annotation { "Feature Type Name" : "Feature", "Feature Type Description" : "" }
export const myFeature = defineFeature(function(context is Context, id is Id, definition is map)
    precondition{}
    {
        {
            var Q0;
            Q0=qCreatedBy(makeId("Front.planeOp"),FACE);
            var sketch = newSketch(context, id + "F0", { "sketchPlane" : qUnion([Q0])});
            skLineSegment(sketch, "E0", {"start": v(-28.04, -14.03) * mm, "end": v(-24.95, -14.03) * mm});
            skLineSegment(sketch, "E1", {"start": v(-24.95, -14.03) * mm, "end": v(-22.4, -16.57) * mm});
            skLineSegment(sketch, "E2", {"start": v(-22.4, -16.57) * mm, "end": v(-22.4, -21.02) * mm});
            skLineSegment(sketch, "E3", {"start": v(-22.4, -21.02) * mm, "end": v(-24.95, -23.56) * mm});
            skLineSegment(sketch, "E4", {"start": v(-24.95, -23.56) * mm, "end": v(-40.78, -23.56) * mm});
            skLineSegment(sketch, "E5", {"start": v(-40.78, -23.56) * mm, "end": v(-40.78, -46.8) * mm});
            skLineSegment(sketch, "E6", {"start": v(0, 62.15) * mm, "end": v(0, 0) * mm, "construction": true});
            skLineSegment(sketch, "E7.MirrorCS", {"start": v(22.4, -21.02) * mm, "end": v(24.95, -23.56) * mm});
            skLineSegment(sketch, "E8.MirrorCS", {"start": v(24.95, -14.03) * mm, "end": v(22.4, -16.57) * mm});
            skLineSegment(sketch, "E9.MirrorCS", {"start": v(22.4, -16.57) * mm, "end": v(22.4, -21.02) * mm});
            skLineSegment(sketch, "E10.MirrorCS", {"start": v(40.78, -23.56) * mm, "end": v(40.78, -46.8) * mm});
            skLineSegment(sketch, "E11.MirrorCS", {"start": v(24.95, -23.56) * mm, "end": v(40.78, -23.56) * mm});
            skLineSegment(sketch, "E12.MirrorCS", {"start": v(28.04, -14.03) * mm, "end": v(24.95, -14.03) * mm});
            skArc(sketch, "E13.trimOffspring", {"start": v(40.73, -1.93) * mm, "mid": v(0, 40.78) * mm, "end": v(-40.73, -1.93) * mm});
            skPoint(sketch, "E14.center.orphan", {"position": v(0, 19.4) * mm});
            skLineSegment(sketch, "E15", {"start": v(-40.78, -46.8) * mm, "end": v(40.78, -46.8) * mm});
            skPoint(sketch, "E16.visualSharp", {"position": v(-38.29, -14.03) * mm});
            skArc(sketch, "E16.filletArc", {"start": v(-40.73, -1.93) * mm, "mid": v(-36.8, -10.52) * mm, "end": v(-28.04, -14.03) * mm});
            skPoint(sketch, "E17.visualSharp", {"position": v(38.29, -14.03) * mm});
            skArc(sketch, "E17.filletArc", {"start": v(28.04, -14.03) * mm, "mid": v(36.8, -10.52) * mm, "end": v(40.73, -1.93) * mm});
            skLineSegment(sketch, "E18", {"start": v(137.49, -46.8) * mm, "end": v(137.49, 16.7) * mm, "construction": true});
            skSolve(sketch);
        }
        {
            var Q0;
            Q0 = qSketchRegion(id + "F0", true);
            var Q1;
            Q1=sQuery(id+"F0.wireOp",EDGE,"E18");
            revolve(context, id + "F1", {"entities" : qUnion([Q0]), "axis" : qUnion([Q1]), "revolveType" : RevolveType.ONE_DIRECTION, "oppositeDirection" : true, "angle" : 180 * degree});
        }
        {
            var Q0;
            Q0=makeQuery(id+"F1.opRevolve","SWEPT_FACE",FACE,{"disambiguationData":[OSD([sQuery(id+"F0.wireOp",EDGE,"E15")])]});
            var sketch = newSketch(context, id + "F2", { "sketchPlane" : qUnion([Q0])});
            skCircle(sketch, "E19", {"center": v(137.49, 0) * mm, "radius": 137.49 * mm});
            skLineSegment(sketch, "E20", {"start": v(6.12, -40.55) * mm, "end": v(268.86, -40.55) * mm, "construction": true});
            skSolve(sketch);
        }
        {
            var Q0;
            Q0=qCreatedBy(makeId("Front.planeOp"),FACE);
            var Q1;
            Q1=sQuery(id+"F2.wireOp",VERTEX,"E20.start");
            cPlane(context, id + "F3", {"entities" : qUnion([Q0, Q1]), "cplaneType" : CPlaneType.PLANE_POINT, "offset" : 25.4 * mm, "width" : 152.4 * mm, "height" : 152.4 * mm});
        }
        {
            var Q0;
            Q0=qCreatedBy(id+"F3.planeOp",FACE);
            var sketch = newSketch(context, id + "F4", { "sketchPlane" : qUnion([Q0])});
            skLineSegment(sketch, "E21", {"start": v(6.12, -656.4) * mm, "end": v(37.87, -656.4) * mm});
            skLineSegment(sketch, "E22", {"start": v(37.87, -490.96) * mm, "end": v(37.87, -479.32) * mm});
            skLineSegment(sketch, "E23", {"start": v(37.87, -479.32) * mm, "end": v(20.16, -479.32) * mm});
            skLineSegment(sketch, "E24", {"start": v(20.16, -479.32) * mm, "end": v(20.16, -472.97) * mm});
            skLineSegment(sketch, "E25", {"start": v(23.58, -104.7) * mm, "end": v(23.58, -67.5) * mm});
            skLineSegment(sketch, "E26", {"start": v(24.77, -46.8) * mm, "end": v(6.12, -46.8) * mm});
            skLineSegment(sketch, "E27", {"start": v(6.12, -46.8) * mm, "end": v(6.12, -172.24) * mm});
            skLineSegment(sketch, "E28", {"start": v(6.12, -172.24) * mm, "end": v(6.12, -223.86) * mm});
            skLineSegment(sketch, "E29", {"start": v(6.12, -223.86) * mm, "end": v(6.12, -342.51) * mm});
            skArc(sketch, "E30", {"start": v(23.58, -104.7) * mm, "mid": v(37.75, -128.48) * mm, "end": v(27.88, -154.34) * mm});
            skArc(sketch, "E31", {"start": v(27.88, -193.2) * mm, "mid": v(37.82, -218) * mm, "end": v(25.3, -241.61) * mm});
            skArc(sketch, "E32.filletArc", {"start": v(27.88, -154.34) * mm, "mid": v(19.48, -173.77) * mm, "end": v(27.88, -193.2) * mm});
            skLineSegment(sketch, "E33", {"start": v(31.58, -59.5) * mm, "end": v(32.79, -59.5) * mm});
            skLineSegment(sketch, "E34", {"start": v(37.87, -54.42) * mm, "end": v(37.87, -51.88) * mm});
            skLineSegment(sketch, "E35", {"start": v(32.79, -46.8) * mm, "end": v(6.12, -46.8) * mm});
            skPoint(sketch, "E36.visualSharp", {"position": v(37.87, -46.8) * mm});
            skArc(sketch, "E36.filletArc", {"start": v(37.87, -51.88) * mm, "mid": v(36.38, -48.29) * mm, "end": v(32.79, -46.8) * mm});
            skPoint(sketch, "E37.visualSharp", {"position": v(37.87, -59.5) * mm});
            skArc(sketch, "E37.filletArc", {"start": v(32.79, -59.5) * mm, "mid": v(36.38, -58.01) * mm, "end": v(37.87, -54.42) * mm});
            skArc(sketch, "E38.filletArc", {"start": v(31.58, -59.5) * mm, "mid": v(25.92, -61.85) * mm, "end": v(23.58, -67.5) * mm});
            skLineSegment(sketch, "E39", {"start": v(37.87, -490.96) * mm, "end": v(20.16, -490.96) * mm});
            skLineSegment(sketch, "E40", {"start": v(20.16, -490.96) * mm, "end": v(20.16, -508.7) * mm});
            skLineSegment(sketch, "E41", {"start": v(28.17, -516.7) * mm, "end": v(37.87, -516.7) * mm});
            skLineSegment(sketch, "E42", {"start": v(37.87, -516.7) * mm, "end": v(37.87, -656.4) * mm});
            skPoint(sketch, "E43.visualSharp", {"position": v(20.16, -516.7) * mm});
            skArc(sketch, "E43.filletArc", {"start": v(20.16, -508.7) * mm, "mid": v(22.5, -514.36) * mm, "end": v(28.17, -516.7) * mm});
            skLineSegment(sketch, "E44", {"start": v(20.16, -466.62) * mm, "end": v(30.25, -466.62) * mm, "construction": true});
            skLineSegment(sketch, "E45", {"start": v(30.25, -466.62) * mm, "end": v(30.25, -472.97) * mm});
            skLineSegment(sketch, "E46", {"start": v(30.25, -472.97) * mm, "end": v(20.16, -472.97) * mm});
            skArc(sketch, "E47", {"start": v(30.25, -466.62) * mm, "mid": v(33.2, -465.62) * mm, "end": v(34.91, -463.02) * mm});
            skArc(sketch, "E48", {"start": v(34.91, -463.02) * mm, "mid": v(41.17, -415.37) * mm, "end": v(35.3, -367.66) * mm});
            skArc(sketch, "E49", {"start": v(35.3, -367.66) * mm, "mid": v(24.95, -305.06) * mm, "end": v(25.3, -241.61) * mm});
            skLineSegment(sketch, "E50", {"start": v(6.12, -342.51) * mm, "end": v(6.12, -656.4) * mm});
            skLineSegment(sketch, "E51", {"start": v(6.12, -656.4) * mm, "end": v(6.12, -721.25) * mm, "construction": true});
            skPoint(sketch, "E52.start.orphan", {"position": v(-12.54, -46.8) * mm});
            skLineSegment(sketch, "E53", {"start": v(133.47, -162.04) * mm, "end": v(133.47, -223.13) * mm, "construction": true});
            skSolve(sketch);
        }
        {
            var Q0;
            Q0 = qSketchRegion(id + "F4", true);
            var Q1;
            Q1=sQuery(id+"F4.wireOp",EDGE,"E51");
            revolve(context, id + "F5", {"entities" : qUnion([Q0]), "axis" : qUnion([Q1]), "revolveType" : RevolveType.FULL});
        }
        {
            var Q0;
            Q0=makeQuery(id+"F5.opRevolve","SWEPT_FACE",FACE,{"disambiguationData":[OSD([sQuery(id+"F4.wireOp",EDGE,"E40")])]});
            var Q1;
            Q1=makeQuery(id+"F5.opRevolve","SWEPT_EDGE",EDGE,{"disambiguationData":[OSD([sQuery(id+"F4.wireOp",EDGE,"E22"),sQuery(id+"F4.wireOp",EDGE,"E39")])]});
            var Q2;
            Q2=makeQuery(id+"F5.opRevolve","SWEPT_EDGE",EDGE,{"disambiguationData":[OSD([sQuery(id+"F4.wireOp",EDGE,"E22"),sQuery(id+"F4.wireOp",EDGE,"E23")])]});
            fillet(context, id + "F6", {"entities" : qUnion([Q0, Q1, Q2]), "radius" : 2.3 * mm, "tangentPropagation" : true, "allowEdgeOverflow" : false});
        }
        {
            var Q0;
            Q0=qCreatedBy(makeId("Front.planeOp"),FACE);
            var sketch = newSketch(context, id + "F7", { "sketchPlane" : qUnion([Q0])});
            skLineSegment(sketch, "E54.0", {"start": v(274.98, -46.8) * mm, "end": v(0, -46.8) * mm, "construction": true});
            skLineSegment(sketch, "E55", {"start": v(137.49, -46.8) * mm, "end": v(137.49, 87.47) * mm, "construction": true});
            skSolve(sketch);
        }
        {
            var Q0;
            Q0=makeQuery(id+"F5.opRevolve","SWEPT_BODY",BODY,{"disambiguationData":[OSD([sQuery(id+"F4.wireOp",EDGE,"E21"),sQuery(id+"F4.wireOp",EDGE,"E22"),sQuery(id+"F4.wireOp",EDGE,"E23"),sQuery(id+"F4.wireOp",EDGE,"E24"),sQuery(id+"F4.wireOp",EDGE,"E25"),sQuery(id+"F4.wireOp",EDGE,"E27"),sQuery(id+"F4.wireOp",EDGE,"E28"),sQuery(id+"F4.wireOp",EDGE,"E29"),sQuery(id+"F4.wireOp",EDGE,"E30"),sQuery(id+"F4.wireOp",EDGE,"E31"),sQuery(id+"F4.wireOp",EDGE,"E32.filletArc"),sQuery(id+"F4.wireOp",EDGE,"E33"),sQuery(id+"F4.wireOp",EDGE,"E34"),sQuery(id+"F4.wireOp",EDGE,"E35"),sQuery(id+"F4.wireOp",EDGE,"E36.filletArc"),sQuery(id+"F4.wireOp",EDGE,"E37.filletArc"),sQuery(id+"F4.wireOp",EDGE,"E38.filletArc"),sQuery(id+"F4.wireOp",EDGE,"E39"),sQuery(id+"F4.wireOp",EDGE,"E40"),sQuery(id+"F4.wireOp",EDGE,"E41"),sQuery(id+"F4.wireOp",EDGE,"E42"),sQuery(id+"F4.wireOp",EDGE,"E43.filletArc"),sQuery(id+"F4.wireOp",EDGE,"E45"),sQuery(id+"F4.wireOp",EDGE,"E46"),sQuery(id+"F4.wireOp",EDGE,"E47"),sQuery(id+"F4.wireOp",EDGE,"E48"),sQuery(id+"F4.wireOp",EDGE,"E49"),sQuery(id+"F4.wireOp",EDGE,"E50")])]});
            var Q1;
            Q1=sQuery(id+"F7.wireOp",EDGE,"E55");
            circularPattern(context, id + "F8", {"entities" : qUnion([Q0]), "axis" : qUnion([Q1]), "angle" : 145.7 * degree, "instanceCount" : 4, "oppositeDirection" : true, "equalSpace" : true});
        }
        {
            var Q0;
            Q0=qCreatedBy(makeId("Front.planeOp"),FACE);
            var sketch = newSketch(context, id + "F9", { "sketchPlane" : qUnion([Q0])});
            skText(sketch, "E56", { "text": "Berrocal Hand-Railings", "fontName": "OpenSans-Bold.ttf"});
            skLineSegment(sketch, "E57", {"start": v(0, -46.7) * mm, "end": v(0, -39.57) * mm, "construction": true});
            const initialGuessF9  = {"E56": [-0.03175, -0.03957, 1, 0, 0.00402]};
            skSetInitialGuess(sketch, initialGuessF9);
            skSolve(sketch);
        }
        {
            var Q0;
            Q0 = qSketchRegion(id + "F9", true);
            extrude(context, id + "F10", {"entities" : qUnion([Q0]), "operationType" : NewBodyOperationType.REMOVE, "oppositeDirection" : true, "depth" : 0.64 * mm});
        }
    });